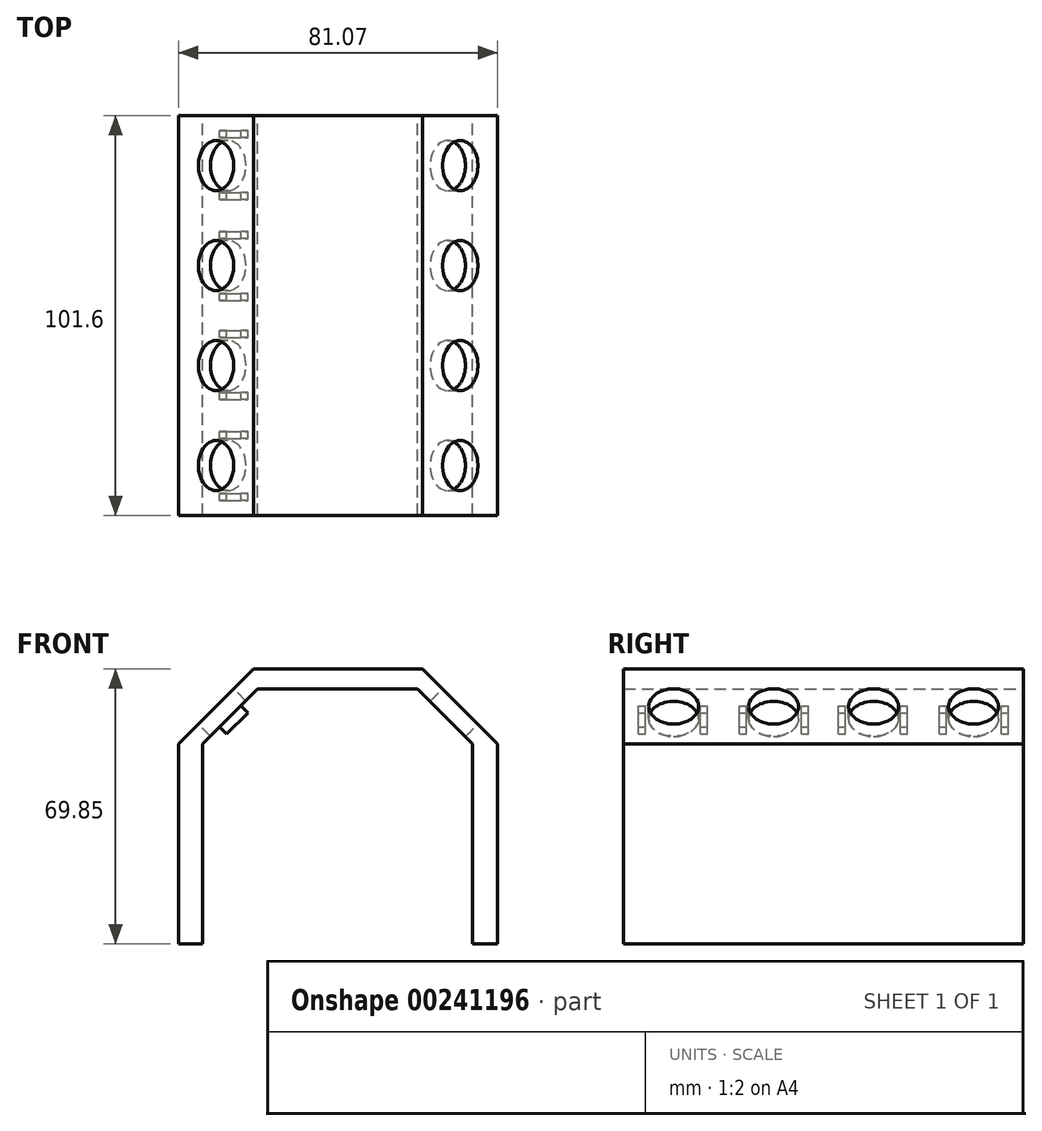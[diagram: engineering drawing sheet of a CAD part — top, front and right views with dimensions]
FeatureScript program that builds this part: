
annotation { "Feature Type Name" : "Feature", "Feature Type Description" : "" }
export const myFeature = defineFeature(function(context is Context, id is Id, definition is map)
    precondition{}
    {
        {
            var Q0;
            Q0=qCreatedBy(makeId("Front.planeOp"),FACE);
            var sketch = newSketch(context, id + "F0", { "sketchPlane" : qUnion([Q0])});
            skLineSegment(sketch, "E0.bottom", {"start": v(19.05, 69.85) * mm, "end": v(62.02, 69.85) * mm});
            skLineSegment(sketch, "E0.left", {"start": v(0, 50.8) * mm, "end": v(0, 0) * mm});
            skLineSegment(sketch, "E0.right", {"start": v(81.07, 50.8) * mm, "end": v(81.07, 0) * mm});
            skLineSegment(sketch, "E1", {"start": v(0, 50.8) * mm, "end": v(19.05, 69.85) * mm});
            skLineSegment(sketch, "E2", {"start": v(62.02, 69.85) * mm, "end": v(81.07, 50.8) * mm});
            skLineSegment(sketch, "E3", {"start": v(6.14, 0) * mm, "end": v(6.14, 50.8) * mm});
            skLineSegment(sketch, "E4", {"start": v(6.14, 50.8) * mm, "end": v(20.11, 64.77) * mm});
            skLineSegment(sketch, "E5", {"start": v(20.11, 64.77) * mm, "end": v(60.75, 64.77) * mm});
            skLineSegment(sketch, "E6", {"start": v(60.75, 64.77) * mm, "end": v(74.72, 50.8) * mm});
            skLineSegment(sketch, "E7", {"start": v(74.72, 50.8) * mm, "end": v(74.72, 0) * mm});
            skLineSegment(sketch, "E8", {"start": v(74.72, 0) * mm, "end": v(81.07, 0) * mm});
            skLineSegment(sketch, "E9", {"start": v(0, 0) * mm, "end": v(6.14, 0) * mm});
            skLineSegment(sketch, "E10", {"start": v(62.02, 69.85) * mm, "end": v(81.07, 69.85) * mm, "construction": true});
            skLineSegment(sketch, "E11", {"start": v(81.07, 50.8) * mm, "end": v(81.07, 69.85) * mm, "construction": true});
            skLineSegment(sketch, "E12", {"start": v(19.05, 69.85) * mm, "end": v(0, 69.85) * mm, "construction": true});
            skLineSegment(sketch, "E13", {"start": v(0, 69.85) * mm, "end": v(0, 50.8) * mm, "construction": true});
            skLineSegment(sketch, "E14", {"start": v(0, 50.8) * mm, "end": v(81.07, 50.8) * mm, "construction": true});
            skSolve(sketch);
        }
        {
            var Q0;
            Q0 = qSketchRegion(id + "F0", true);
            extrude(context, id + "F1", {"entities" : qUnion([Q0]), "depth" : 101.6 * mm});
        }
        {
            var Q0;
            Q0=makeQuery(id+"F1.opExtrude","SWEPT_FACE",FACE,{"disambiguationData":[OSD([sQuery(id+"F0.wireOp",EDGE,"E2")])]});
            var sketch = newSketch(context, id + "F2", { "sketchPlane" : qUnion([Q0])});
            skCircle(sketch, "E15", {"center": v(-12.7, -7.94) * mm, "radius": 6.35 * mm});
            skCircle(sketch, "E16", {"center": v(-38.1, -7.94) * mm, "radius": 6.35 * mm});
            skCircle(sketch, "E17", {"center": v(-63.5, -7.94) * mm, "radius": 6.35 * mm});
            skCircle(sketch, "E18", {"center": v(-88.9, -7.94) * mm, "radius": 6.35 * mm});
            skLineSegment(sketch, "E19", {"start": v(0, -7.94) * mm, "end": v(-101.6, -7.94) * mm, "construction": true});
            skSolve(sketch);
        }
        {
            var Q0;
            Q0 = qSketchRegion(id + "F2", true);
            extrude(context, id + "F3", {"entities" : qUnion([Q0]), "operationType" : NewBodyOperationType.REMOVE, "oppositeDirection" : true, "depth" : 25.4 * mm});
        }
        {
            var Q0;
            Q0=makeQuery(id+"F1.opExtrude","SWEPT_FACE",FACE,{"disambiguationData":[OSD([sQuery(id+"F0.wireOp",EDGE,"E1")])]});
            var sketch = newSketch(context, id + "F4", { "sketchPlane" : qUnion([Q0])});
            skCircle(sketch, "E20", {"center": v(88.9, 49.4) * mm, "radius": 6.35 * mm});
            skCircle(sketch, "E21", {"center": v(63.5, 49.4) * mm, "radius": 6.35 * mm});
            skCircle(sketch, "E22", {"center": v(38.1, 49.4) * mm, "radius": 6.35 * mm});
            skCircle(sketch, "E23", {"center": v(12.7, 49.4) * mm, "radius": 6.35 * mm});
            skLineSegment(sketch, "E24", {"start": v(101.6, 49.4) * mm, "end": v(0, 49.4) * mm, "construction": true});
            skSolve(sketch);
        }
        {
            var Q0;
            Q0 = qSketchRegion(id + "F4", true);
            extrude(context, id + "F5", {"entities" : qUnion([Q0]), "operationType" : NewBodyOperationType.REMOVE, "oppositeDirection" : true, "depth" : 25.4 * mm});
        }
        {
            var Q0;
            Q0=makeQuery(id+"F1.opExtrude","SWEPT_FACE",FACE,{"disambiguationData":[OSD([sQuery(id+"F0.wireOp",EDGE,"E4")])]});
            var sketch = newSketch(context, id + "F6", { "sketchPlane" : qUnion([Q0])});
            skLineSegment(sketch, "E25.bottom", {"start": v(-97.8, 46.33) * mm, "end": v(-96.01, 46.33) * mm});
            skLineSegment(sketch, "E25.top", {"start": v(-97.8, 53.95) * mm, "end": v(-96.01, 53.95) * mm});
            skLineSegment(sketch, "E25.left", {"start": v(-97.8, 46.33) * mm, "end": v(-97.8, 53.95) * mm});
            skLineSegment(sketch, "E25.right", {"start": v(-96.01, 46.33) * mm, "end": v(-96.01, 53.95) * mm});
            skLineSegment(sketch, "E26.bottom", {"start": v(-82.04, 46.33) * mm, "end": v(-80.26, 46.33) * mm});
            skLineSegment(sketch, "E26.top", {"start": v(-82.04, 53.95) * mm, "end": v(-80.26, 53.95) * mm});
            skLineSegment(sketch, "E26.left", {"start": v(-82.04, 46.33) * mm, "end": v(-82.04, 53.95) * mm});
            skLineSegment(sketch, "E26.right", {"start": v(-80.26, 46.33) * mm, "end": v(-80.26, 53.95) * mm});
            skLineSegment(sketch, "E27.bottom", {"start": v(-72.14, 46.33) * mm, "end": v(-70.36, 46.33) * mm});
            skLineSegment(sketch, "E27.top", {"start": v(-72.14, 53.95) * mm, "end": v(-70.36, 53.95) * mm});
            skLineSegment(sketch, "E27.left", {"start": v(-72.14, 46.33) * mm, "end": v(-72.14, 53.95) * mm});
            skLineSegment(sketch, "E27.right", {"start": v(-70.36, 46.33) * mm, "end": v(-70.36, 53.95) * mm});
            skLineSegment(sketch, "E28.bottom", {"start": v(-56.39, 46.33) * mm, "end": v(-54.6, 46.33) * mm});
            skLineSegment(sketch, "E28.top", {"start": v(-56.39, 53.95) * mm, "end": v(-54.6, 53.95) * mm});
            skLineSegment(sketch, "E28.left", {"start": v(-56.39, 46.33) * mm, "end": v(-56.39, 53.95) * mm});
            skLineSegment(sketch, "E28.right", {"start": v(-54.6, 46.33) * mm, "end": v(-54.6, 53.95) * mm});
            skLineSegment(sketch, "E29.bottom", {"start": v(-46.99, 46.33) * mm, "end": v(-45.21, 46.33) * mm});
            skLineSegment(sketch, "E29.top", {"start": v(-46.99, 53.95) * mm, "end": v(-45.21, 53.95) * mm});
            skLineSegment(sketch, "E29.left", {"start": v(-46.99, 46.33) * mm, "end": v(-46.99, 53.95) * mm});
            skLineSegment(sketch, "E29.right", {"start": v(-45.21, 46.33) * mm, "end": v(-45.21, 53.95) * mm});
            skLineSegment(sketch, "E30.bottom", {"start": v(-31.24, 46.33) * mm, "end": v(-29.46, 46.33) * mm});
            skLineSegment(sketch, "E30.top", {"start": v(-31.24, 53.95) * mm, "end": v(-29.46, 53.95) * mm});
            skLineSegment(sketch, "E30.left", {"start": v(-31.24, 46.33) * mm, "end": v(-31.24, 53.95) * mm});
            skLineSegment(sketch, "E30.right", {"start": v(-29.46, 46.33) * mm, "end": v(-29.46, 53.95) * mm});
            skLineSegment(sketch, "E31.bottom", {"start": v(-21.34, 46.33) * mm, "end": v(-19.56, 46.33) * mm});
            skLineSegment(sketch, "E31.top", {"start": v(-21.34, 53.95) * mm, "end": v(-19.56, 53.95) * mm});
            skLineSegment(sketch, "E31.left", {"start": v(-21.34, 46.33) * mm, "end": v(-21.34, 53.95) * mm});
            skLineSegment(sketch, "E31.right", {"start": v(-19.56, 46.33) * mm, "end": v(-19.56, 53.95) * mm});
            skLineSegment(sketch, "E32.bottom", {"start": v(-5.59, 46.33) * mm, "end": v(-3.8, 46.33) * mm});
            skLineSegment(sketch, "E32.top", {"start": v(-5.59, 53.95) * mm, "end": v(-3.8, 53.95) * mm});
            skLineSegment(sketch, "E32.left", {"start": v(-5.59, 46.33) * mm, "end": v(-5.59, 53.95) * mm});
            skLineSegment(sketch, "E32.right", {"start": v(-3.8, 46.33) * mm, "end": v(-3.8, 53.95) * mm});
            skLineSegment(sketch, "E33", {"start": v(-3.8, 53.95) * mm, "end": v(-97.8, 53.95) * mm, "construction": true});
            skLineSegment(sketch, "E34", {"start": v(-96.01, 46.33) * mm, "end": v(-3.8, 46.33) * mm, "construction": true});
            skSolve(sketch);
        }
        {
            var Q0;
            Q0 = qSketchRegion(id + "F6", true);
            extrude(context, id + "F7", {"entities" : qUnion([Q0]), "operationType" : NewBodyOperationType.ADD, "depth" : 2.54 * mm});
        }
    });
